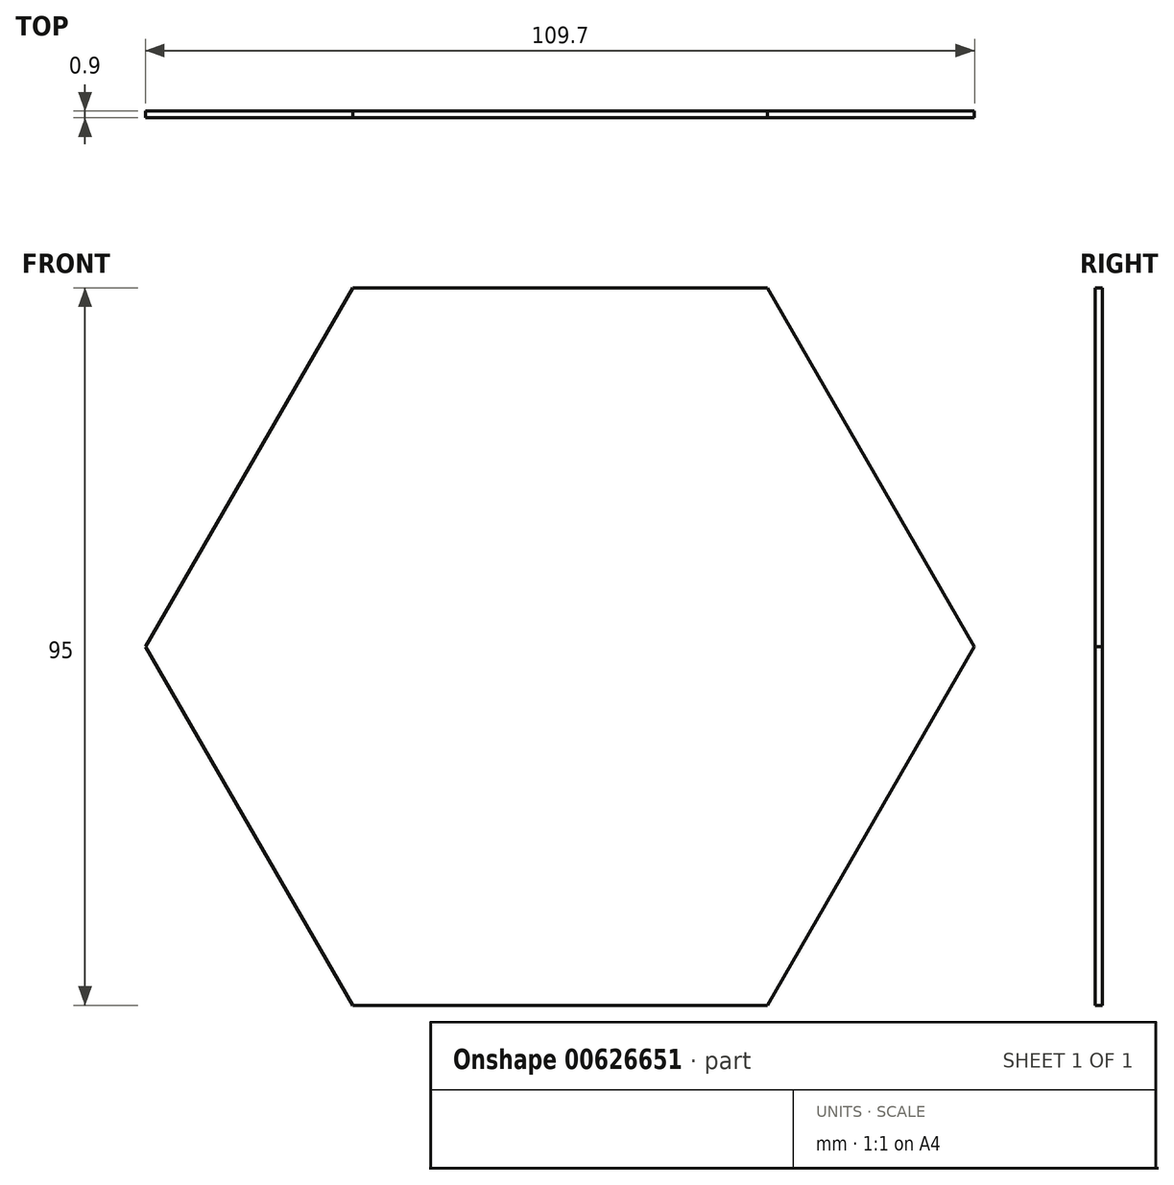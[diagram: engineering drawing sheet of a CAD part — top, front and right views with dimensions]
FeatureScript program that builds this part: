
annotation { "Feature Type Name" : "Feature", "Feature Type Description" : "" }
export const myFeature = defineFeature(function(context is Context, id is Id, definition is map)
    precondition{}
    {
        {
            var Q0;
            Q0=qCreatedBy(makeId("Front.planeOp"),FACE);
            var sketch = newSketch(context, id + "F0", { "sketchPlane" : qUnion([Q0])});
            skCircle(sketch, "E0.cCircle", {"center": v(0, 0) * mm, "radius": 47.5 * mm, "construction": true});
            skLineSegment(sketch, "E0.0", {"start": v(27.42, -47.5) * mm, "end": v(-27.42, -47.5) * mm});
            skLineSegment(sketch, "E0.1", {"start": v(-27.42, -47.5) * mm, "end": v(-54.85, 0) * mm});
            skLineSegment(sketch, "E0.2", {"start": v(-54.85, 0) * mm, "end": v(-27.42, 47.5) * mm});
            skLineSegment(sketch, "E0.3", {"start": v(-27.42, 47.5) * mm, "end": v(27.42, 47.5) * mm});
            skLineSegment(sketch, "E0.4", {"start": v(27.42, 47.5) * mm, "end": v(54.85, 0) * mm});
            skLineSegment(sketch, "E0.5", {"start": v(54.85, 0) * mm, "end": v(27.42, -47.5) * mm});
            skPoint(sketch, "E0.0.midPoint", {"position": v(0, -47.5) * mm});
            skSolve(sketch);
        }
        {
            var Q0;
            Q0 = qSketchRegion(id + "F0", true);
            extrude(context, id + "F1", {"entities" : qUnion([Q0]), "depth" : 0.9 * mm, "offsetDistance" : 25 * mm});
        }
    });
